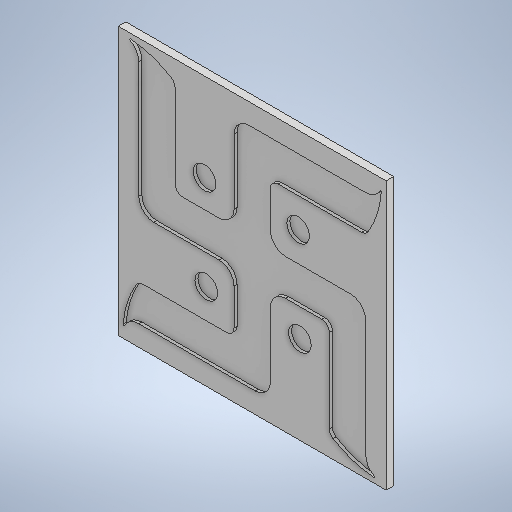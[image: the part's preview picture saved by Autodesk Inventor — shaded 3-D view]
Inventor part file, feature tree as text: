
AUTODESK INVENTOR PART (.ipt)
format: ipt  version: 2025.2 (Build 292293000, 293)  size: 347,648 bytes
history: native  units: in
note: dims shown in document units (in); Inventor stores cm internally (conversion verified against a paired STEP export)
features: sketch x3, extrude x2
ambient origin geometry x8: Origin, YZ Plane, XZ Plane, XY Plane, X Axis, Y Axis, Z Axis, Center Point
bodies: Solid1 (feature_tree)
feature tree (5):
  sketch  "Sketch1"  dims[d3=2.4213in d4=2.4213in d16=5.9055in]
  extrude  "Extrusion1"  Depth=5.9055in
  extrude  "Extrusion2"  Depth=0.9449in
  sketch  "Sketch Circular Pattern1"  dims[d17=5.9055in d18=0.9449in]
  sketch  "Sketch Circular Pattern2"  dims[d19=0.9449in d22=2.4803in d23=0.9449in d24=2.4803in d25=0.9449in d28=0.3937in d29=0.1969in d30=0.3937in d31=0.5906in d32=1.5748in d34=360.0deg d36=0.0197in d37=0.1969in d38=1.5748in d40=360.0deg d42=6.9685in d43=6.9685in d44=0.1969in d45=0.0in d46=0.1181in d47=0.0in]
